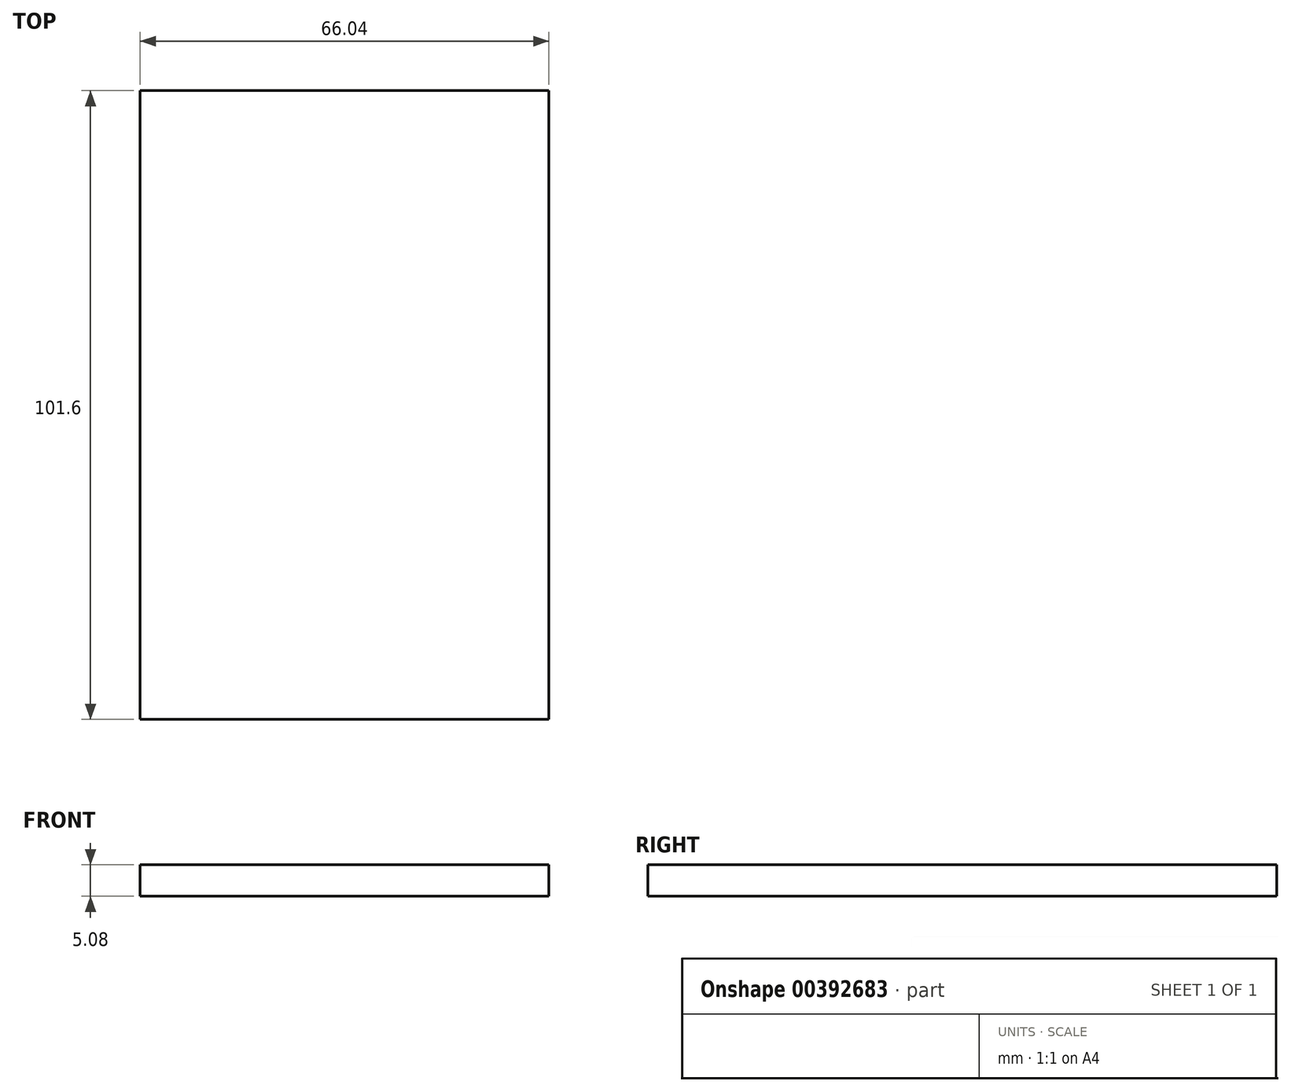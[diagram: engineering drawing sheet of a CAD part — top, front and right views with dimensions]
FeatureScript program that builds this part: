
annotation { "Feature Type Name" : "Feature", "Feature Type Description" : "" }
export const myFeature = defineFeature(function(context is Context, id is Id, definition is map)
    precondition{}
    {
        {
            var Q0;
            Q0=qCreatedBy(makeId("Front.planeOp"),FACE);
            var sketch = newSketch(context, id + "F0", { "sketchPlane" : qUnion([Q0])});
            skLineSegment(sketch, "E0.bottom", {"start": v(-33.02, 2.54) * mm, "end": v(33.02, 2.54) * mm});
            skLineSegment(sketch, "E0.top", {"start": v(-33.02, -2.54) * mm, "end": v(33.02, -2.54) * mm});
            skLineSegment(sketch, "E0.left", {"start": v(-33.02, 2.54) * mm, "end": v(-33.02, -2.54) * mm});
            skLineSegment(sketch, "E0.right", {"start": v(33.02, 2.54) * mm, "end": v(33.02, -2.54) * mm});
            skPoint(sketch, "E0.middle", {"position": v(0, 0) * mm});
            skSolve(sketch);
        }
        {
            var Q0;
            Q0 = qSketchRegion(id + "F0", true);
            extrude(context, id + "F1", {"entities" : qUnion([Q0]), "depth" : 101.6 * mm});
        }
    });
